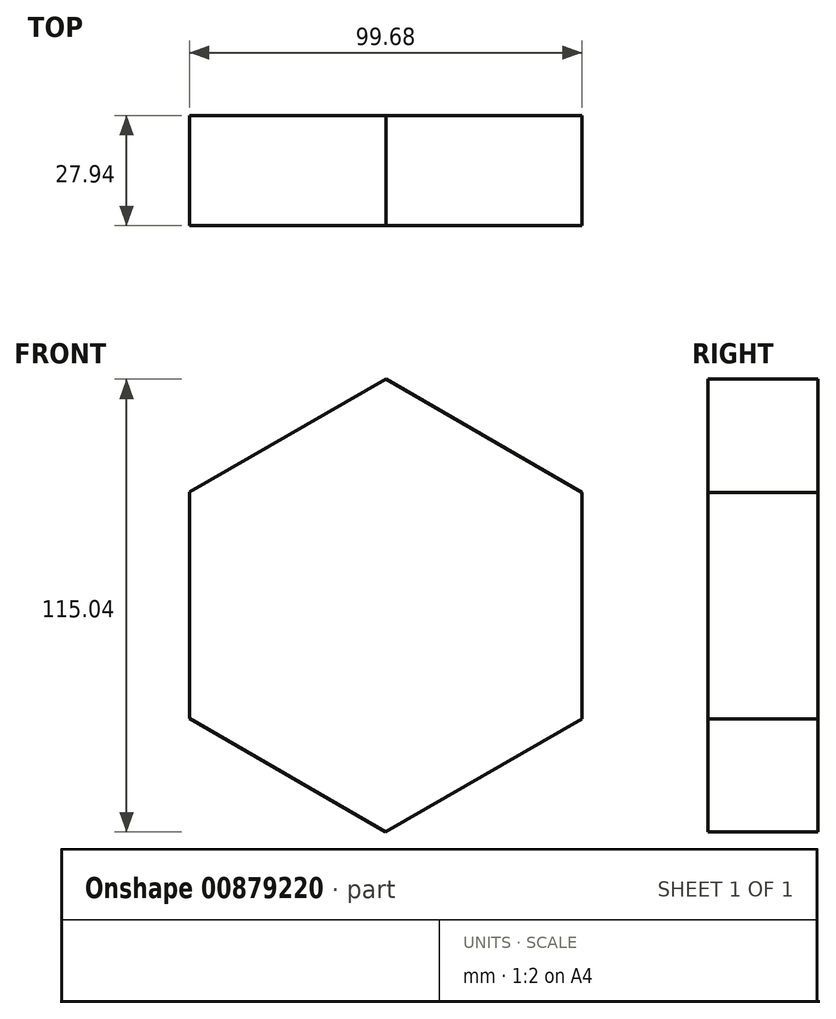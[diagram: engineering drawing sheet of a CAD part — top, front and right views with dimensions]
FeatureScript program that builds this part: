
annotation { "Feature Type Name" : "Feature", "Feature Type Description" : "" }
export const myFeature = defineFeature(function(context is Context, id is Id, definition is map)
    precondition{}
    {
        {
            var Q0;
            Q0=qCreatedBy(makeId("Front.planeOp"),FACE);
            var sketch = newSketch(context, id + "F0", { "sketchPlane" : qUnion([Q0])});
            skCircle(sketch, "E0.cCircle", {"center": v(0, 0) * mm, "radius": 49.82 * mm, "construction": true});
            skLineSegment(sketch, "E0.0", {"start": v(-49.8, 28.8) * mm, "end": v(0.04, 57.52) * mm});
            skLineSegment(sketch, "E0.1", {"start": v(0.04, 57.52) * mm, "end": v(49.84, 28.73) * mm});
            skLineSegment(sketch, "E0.2", {"start": v(49.84, 28.73) * mm, "end": v(49.8, -28.8) * mm});
            skLineSegment(sketch, "E0.3", {"start": v(49.8, -28.8) * mm, "end": v(-0.04, -57.52) * mm});
            skLineSegment(sketch, "E0.4", {"start": v(-0.04, -57.52) * mm, "end": v(-49.84, -28.73) * mm});
            skLineSegment(sketch, "E0.5", {"start": v(-49.84, -28.73) * mm, "end": v(-49.8, 28.8) * mm});
            skPoint(sketch, "E0.0.midPoint", {"position": v(-24.88, 43.16) * mm});
            skSolve(sketch);
        }
        {
            var Q0;
            Q0=makeQuery(id+"F0.imprint","IMPRINT",FACE,{"disambiguationData":[TD([[makeQuery(id+"F0.imprint","IMPRINT",EDGE,{"derivedFrom":sQuery(id+"F0.wireOp",EDGE,"E0.0")}),-1.0]])]});
            extrude(context, id + "F1", {"entities" : qUnion([Q0]), "depth" : 27.94 * mm, "offsetDistance" : 25.4 * mm});
        }
    });
